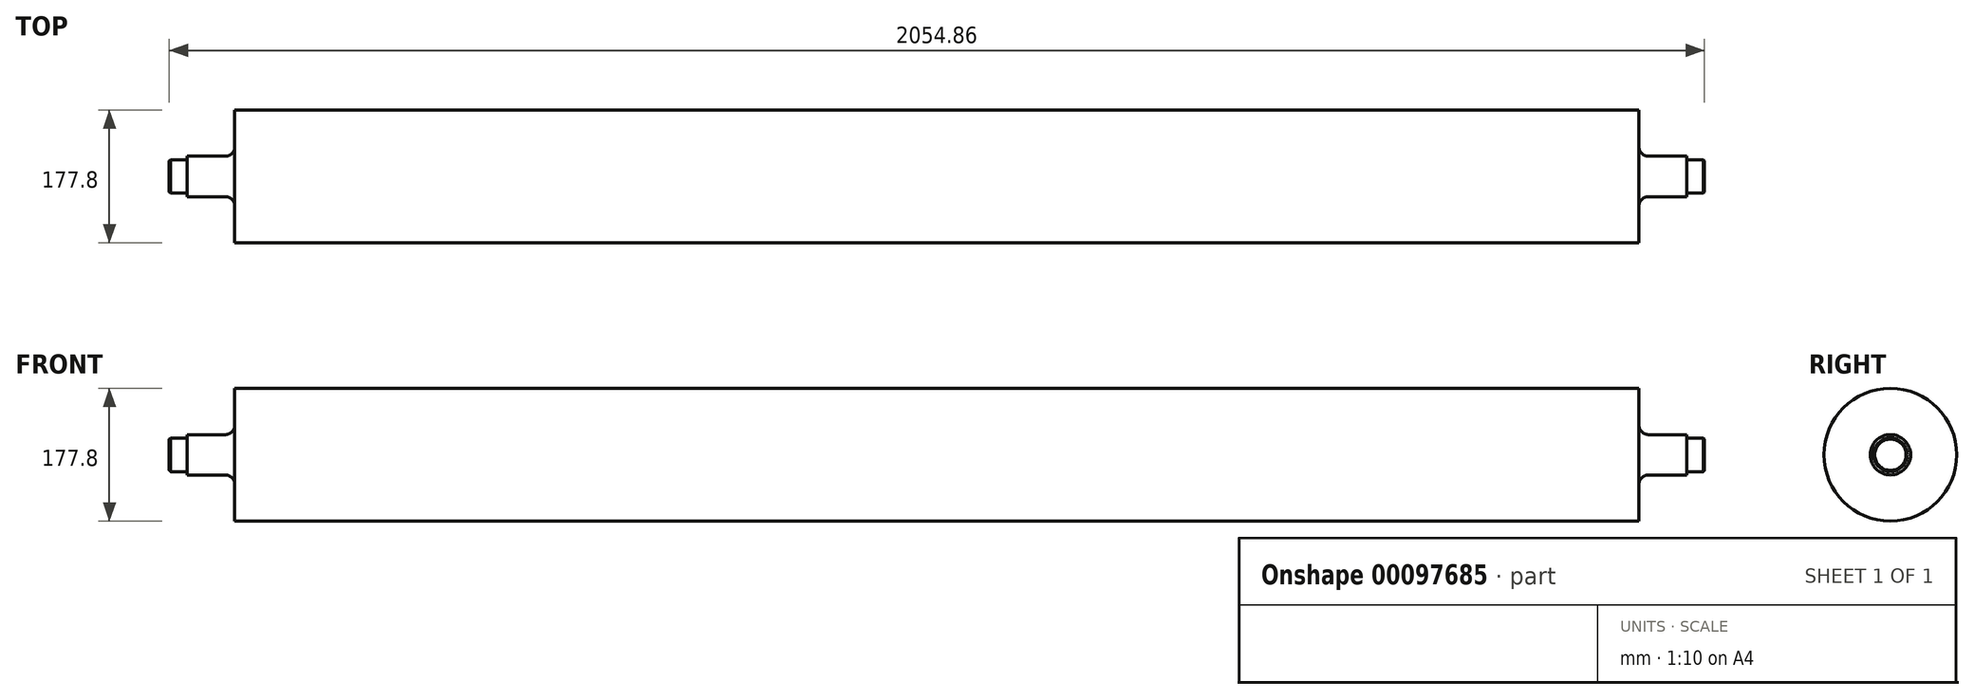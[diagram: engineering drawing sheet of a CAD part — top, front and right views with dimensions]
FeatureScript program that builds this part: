
annotation { "Feature Type Name" : "Feature", "Feature Type Description" : "" }
export const myFeature = defineFeature(function(context is Context, id is Id, definition is map)
    precondition{}
    {
        {
            var Q0;
            Q0=qCreatedBy(makeId("Right.planeOp"),FACE);
            var sketch = newSketch(context, id + "F0", { "sketchPlane" : qUnion([Q0])});
            skCircle(sketch, "E0", {"center": v(0, 0) * mm, "radius": 22.51 * mm});
            skSolve(sketch);
        }
        {
            var Q0;
            Q0=qSketchRegion(id+"F0",true);
            extrude(context, id + "F1", {"entities" : qUnion([Q0]), "endBound" : BoundingType.SYMMETRIC, "depth" : 2054.86 * mm});
        }
        {
            var Q0;
            Q0=qCreatedBy(makeId("Right.planeOp"),FACE);
            var sketch = newSketch(context, id + "F2", { "sketchPlane" : qUnion([Q0])});
            skCircle(sketch, "E1", {"center": v(0, 0) * mm, "radius": 27 * mm});
            skSolve(sketch);
        }
        {
            var Q0;
            Q0=qSketchRegion(id+"F2",true);
            extrude(context, id + "F3", {"entities" : qUnion([Q0]), "operationType" : NewBodyOperationType.ADD, "endBound" : BoundingType.SYMMETRIC, "depth" : 2007.1 * mm});
        }
        {
            var Q0;
            Q0=qCreatedBy(makeId("Right.planeOp"),FACE);
            var sketch = newSketch(context, id + "F4", { "sketchPlane" : qUnion([Q0])});
            skCircle(sketch, "E2", {"center": v(0, 0) * mm, "radius": 88.9 * mm});
            skSolve(sketch);
        }
        {
            var Q0;
            Q0=qSketchRegion(id+"F4",true);
            extrude(context, id + "F5", {"entities" : qUnion([Q0]), "operationType" : NewBodyOperationType.ADD, "endBound" : BoundingType.SYMMETRIC, "depth" : 1879.6 * mm});
        }
        {
            var Q0;
            Q0=makeQuery(id+"F5.boolean.opBoolean","INTERSECT",EDGE,{"derivedFrom":[makeQuery(id+"F3.opExtrude","SWEPT_FACE",FACE,{"disambiguationData":[OSD([sQuery(id+"F2.wireOp",EDGE,"E1")])]}),makeQuery(id+"F5.opExtrude","CAP_FACE",FACE,{"disambiguationData":[OSD([sQuery(id+"F4.wireOp",EDGE,"E2")])],"isStart":false})]});
            var Q1;
            Q1=makeQuery(id+"F5.boolean.opBoolean","INTERSECT",EDGE,{"derivedFrom":[makeQuery(id+"F3.opExtrude","SWEPT_FACE",FACE,{"disambiguationData":[OSD([sQuery(id+"F2.wireOp",EDGE,"E1")])]}),makeQuery(id+"F5.opExtrude","CAP_FACE",FACE,{"disambiguationData":[OSD([sQuery(id+"F4.wireOp",EDGE,"E2")])],"isStart":true})]});
            fillet(context, id + "F6", {"entities" : qUnion([Q0, Q1]), "radius" : 12.7 * mm, "tangentPropagation" : true, "allowEdgeOverflow" : false});
        }
        {
            var Q0;
            Q0=makeQuery(id+"F3.boolean.opBoolean","INTERSECT",EDGE,{"derivedFrom":[makeQuery(id+"F1.opExtrude","SWEPT_FACE",FACE,{"disambiguationData":[OSD([sQuery(id+"F0.wireOp",EDGE,"E0")])]}),makeQuery(id+"F3.opExtrude","CAP_FACE",FACE,{"disambiguationData":[OSD([sQuery(id+"F2.wireOp",EDGE,"E1")])],"isStart":true})]});
            fillet(context, id + "F7", {"entities" : qUnion([Q0]), "radius" : 0.76 * mm, "tangentPropagation" : true, "allowEdgeOverflow" : false});
        }
        {
            var Q0;
            Q0=makeQuery(id+"F3.boolean.opBoolean","INTERSECT",EDGE,{"derivedFrom":[makeQuery(id+"F1.opExtrude","SWEPT_FACE",FACE,{"disambiguationData":[OSD([sQuery(id+"F0.wireOp",EDGE,"E0")])]}),makeQuery(id+"F3.opExtrude","CAP_FACE",FACE,{"disambiguationData":[OSD([sQuery(id+"F2.wireOp",EDGE,"E1")])],"isStart":false})]});
            fillet(context, id + "F8", {"entities" : qUnion([Q0]), "radius" : 0.76 * mm, "tangentPropagation" : true, "allowEdgeOverflow" : false});
        }
        {
            var Q0;
            Q0=makeQuery(id+"F1.opExtrude","CAP_FACE",FACE,{"disambiguationData":[OSD([sQuery(id+"F0.wireOp",EDGE,"E0")])],"isStart":false});
            var Q1;
            Q1=makeQuery(id+"F1.opExtrude","CAP_FACE",FACE,{"disambiguationData":[OSD([sQuery(id+"F0.wireOp",EDGE,"E0")])],"isStart":true});
            chamfer(context, id + "F9", {"entities" : qUnion([Q0, Q1]), "width" : 1.52 * mm, "tangentPropagation" : true});
        }
    });
